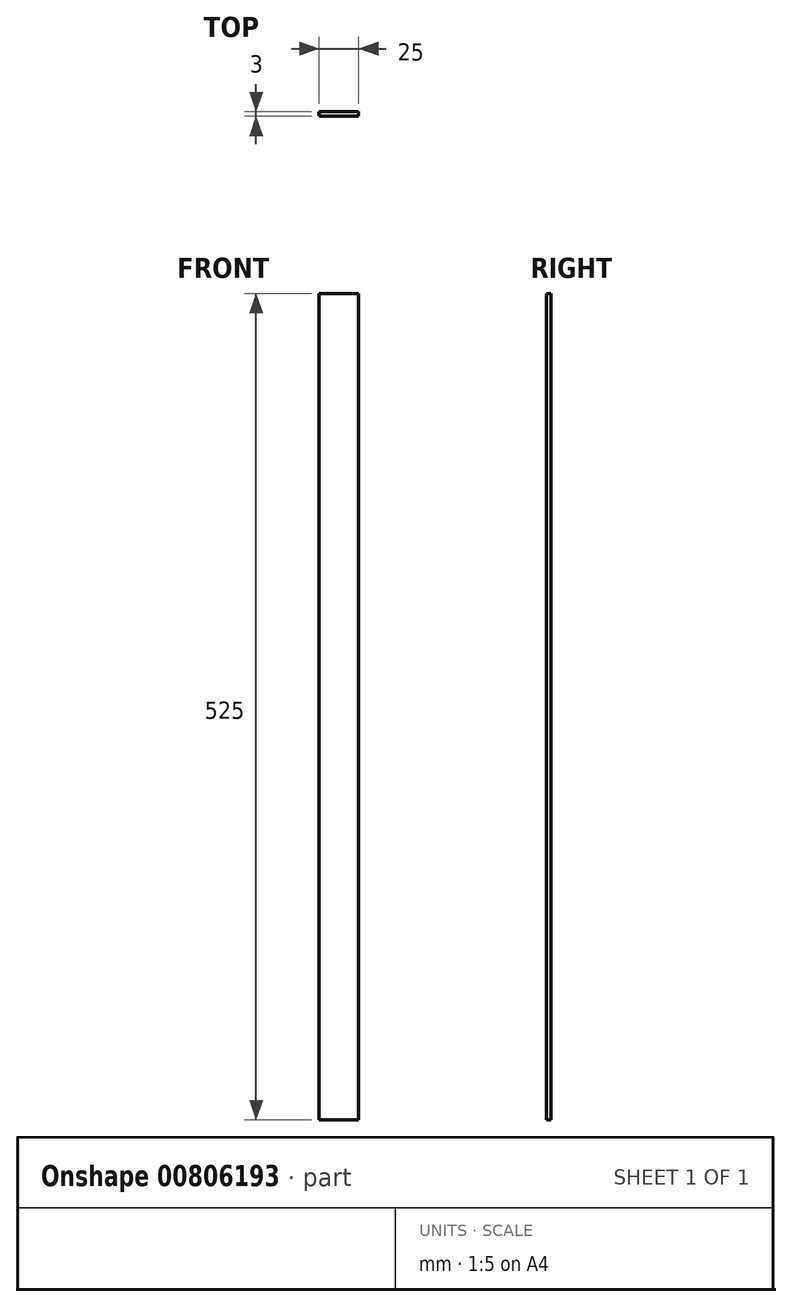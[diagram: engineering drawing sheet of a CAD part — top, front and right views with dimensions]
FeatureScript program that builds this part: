
annotation { "Feature Type Name" : "Feature", "Feature Type Description" : "" }
export const myFeature = defineFeature(function(context is Context, id is Id, definition is map)
    precondition{}
    {
        {
            var Q0;
            Q0=qCreatedBy(makeId("Top.planeOp"),FACE);
            var sketch = newSketch(context, id + "F0", { "sketchPlane" : qUnion([Q0])});
            skLineSegment(sketch, "E0.bottom", {"start": v(0, 0) * mm, "end": v(25, 0) * mm});
            skLineSegment(sketch, "E0.top", {"start": v(0, -3) * mm, "end": v(25, -3) * mm});
            skLineSegment(sketch, "E0.left", {"start": v(0, 0) * mm, "end": v(0, -3) * mm});
            skLineSegment(sketch, "E0.right", {"start": v(25, 0) * mm, "end": v(25, -3) * mm});
            skSolve(sketch);
        }
        {
            var Q0;
            Q0=qSketchRegion(id+"F0",true);
            extrude(context, id + "F1", {"entities" : qUnion([Q0]), "depth" : 525 * mm, "offsetDistance" : 25 * mm});
        }
    });
